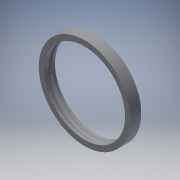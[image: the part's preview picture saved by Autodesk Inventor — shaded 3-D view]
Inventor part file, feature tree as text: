
AUTODESK INVENTOR PART (.ipt)
format: ipt  version: 2017 (Build 210142000, 142)  size: 126,976 bytes
history: native  units: in
note: dims shown in document units (in); Inventor stores cm internally (conversion verified against a paired STEP export)
features: revolve x1, sketch x1
ambient origin geometry x8: Origin, YZ Plane, XZ Plane, XY Plane, X Axis, Y Axis, Z Axis, Center Point
bodies: Solid1 (feature_tree)
feature tree (2):
  revolve  "Revolution1"  [1 undecoded]
  sketch  "Sketch1"  dims[d1=1.875in d2=0.124in d3=0.25in d4=0.25in d5=0.0675in d6=0.135in d7=90.0deg]
note: 1 required parameter value undecoded (feature->parameter linkage not recoverable at this tier; creation-order binding heuristic only, values carry confidence <= 0.55)
